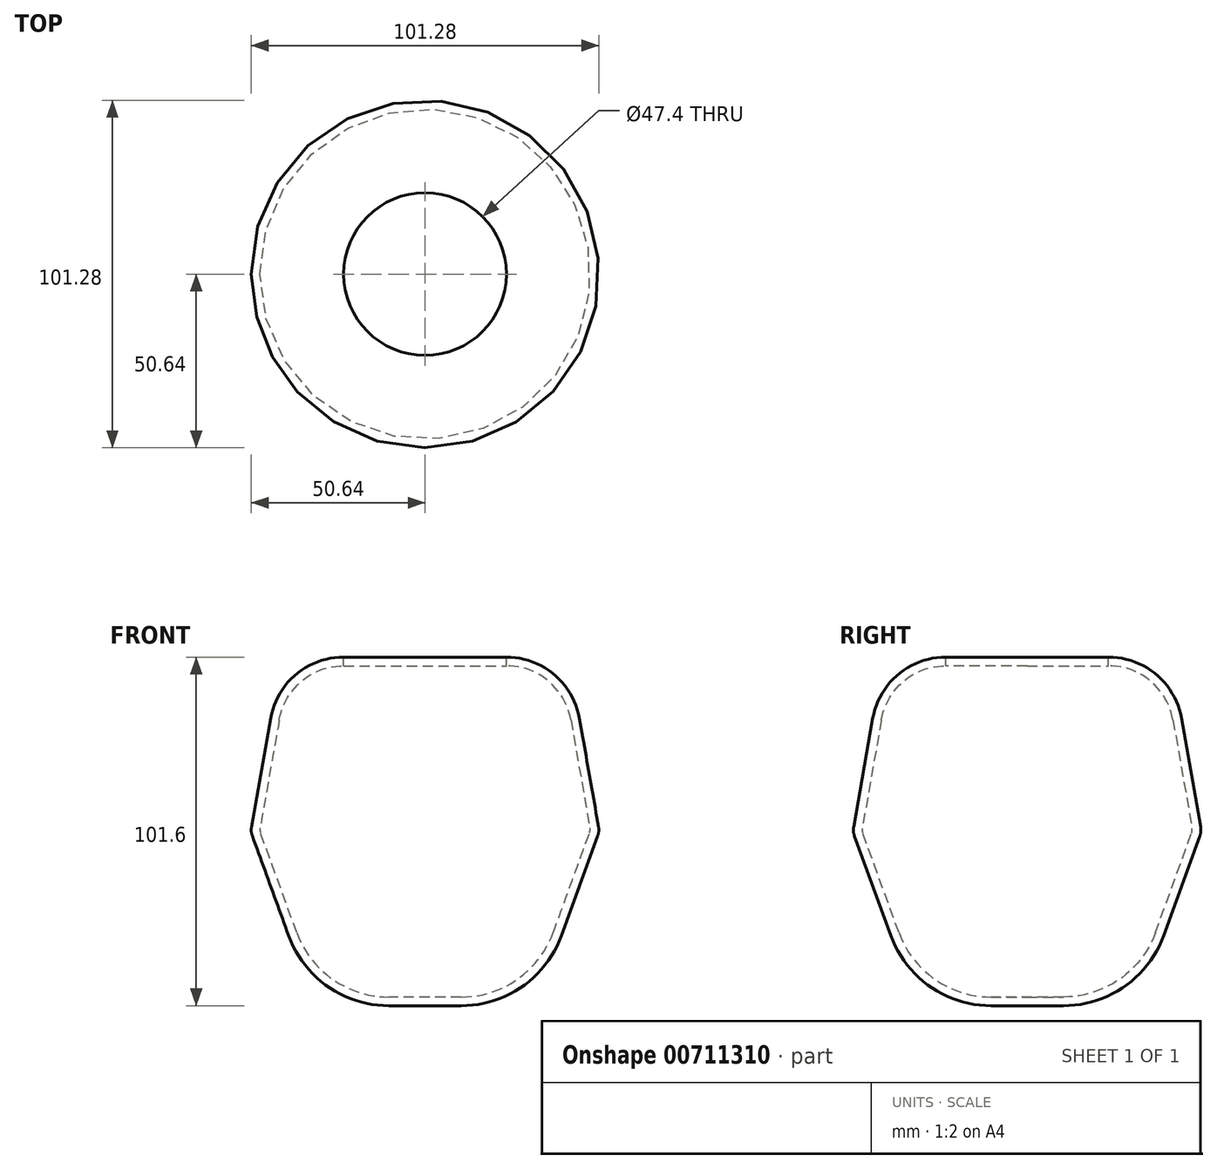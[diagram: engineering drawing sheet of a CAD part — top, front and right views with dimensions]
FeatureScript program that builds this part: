
annotation { "Feature Type Name" : "Feature", "Feature Type Description" : "" }
export const myFeature = defineFeature(function(context is Context, id is Id, definition is map)
    precondition{}
    {
        {
            var Q0;
            Q0=qCreatedBy(makeId("Top.planeOp"),FACE);
            var sketch = newSketch(context, id + "F0", { "sketchPlane" : qUnion([Q0])});
            skCircle(sketch, "E0", {"center": v(0, 0) * mm, "radius": 50.8 * mm});
            skSolve(sketch);
        }
        {
            var Q0;
            Q0=makeQuery(id+"F0.imprint","IMPRINT",FACE,{"disambiguationData":[TD([[makeQuery(id+"F0.imprint","IMPRINT",EDGE,{"derivedFrom":sQuery(id+"F0.wireOp",EDGE,"E0")}),1.0]])]});
            extrude(context, id + "F1", {"entities" : qUnion([Q0]), "depth" : 50.8 * mm, "offsetDistance" : 25.4 * mm, "hasDraft" : true, "draftAngle" : 10 * degree, "draftPullDirection" : true, "hasSecondDirection" : true, "secondDirectionOppositeDirection" : true, "secondDirectionDepth" : 50.8 * mm, "hasSecondDirectionDraft" : true, "secondDirectionDraftAngle" : 20 * degree, "secondDirectionDraftPullDirection" : true});
        }
        {
            var Q0;
            {var subQ0=makeQuery(id+"F1.opExtrude","SWEPT_FACE",FACE,{"disambiguationData":[OSD([sQuery(id+"F0.wireOp",EDGE,"E0")])]});Q0=makeQuery(id+"F1.*.booleanUnion.opBoolean","MERGE",EDGE,{"derivedFrom":[makeQuery(id+"F1.*.split.splitOp","SPLIT_SURFACE_INTERSECT",EDGE,{"derivedFrom":[subQ0]}),makeQuery(id+"F1.*.split.splitOp","SPLIT_SURFACE_INTERSECT",EDGE,{"derivedFrom":[subQ0],"isFromBackBody":true})]});}
            fillet(context, id + "F2", {"entities" : qUnion([Q0]), "radius" : 5.08 * mm, "tangentPropagation" : true, "allowEdgeOverflow" : false});
        }
        {
            var Q0;
            Q0=makeQuery(id+"F1.opExtrude","CAP_EDGE",EDGE,{"disambiguationData":[OSD([sQuery(id+"F0.wireOp",EDGE,"E0")])],"isStart":true});
            fillet(context, id + "F3", {"entities" : qUnion([Q0]), "radius" : 31.06 * mm, "tangentPropagation" : true, "allowEdgeOverflow" : false});
        }
        {
            var Q0;
            Q0=makeQuery(id+"F1.opExtrude","CAP_EDGE",EDGE,{"disambiguationData":[OSD([sQuery(id+"F0.wireOp",EDGE,"E0")])],"isStart":false});
            fillet(context, id + "F4", {"entities" : qUnion([Q0]), "radius" : 21.62 * mm, "tangentPropagation" : true, "allowEdgeOverflow" : false});
        }
        {
            var Q0;
            Q0=makeQuery(id+"F1.opExtrude","CAP_FACE",FACE,{"disambiguationData":[OSD([sQuery(id+"F0.wireOp",EDGE,"E0")])],"isStart":false});
            shell(context, id + "F5", {"entities" : qUnion([Q0]), "thickness" : 2.54 * mm});
        }
    });
